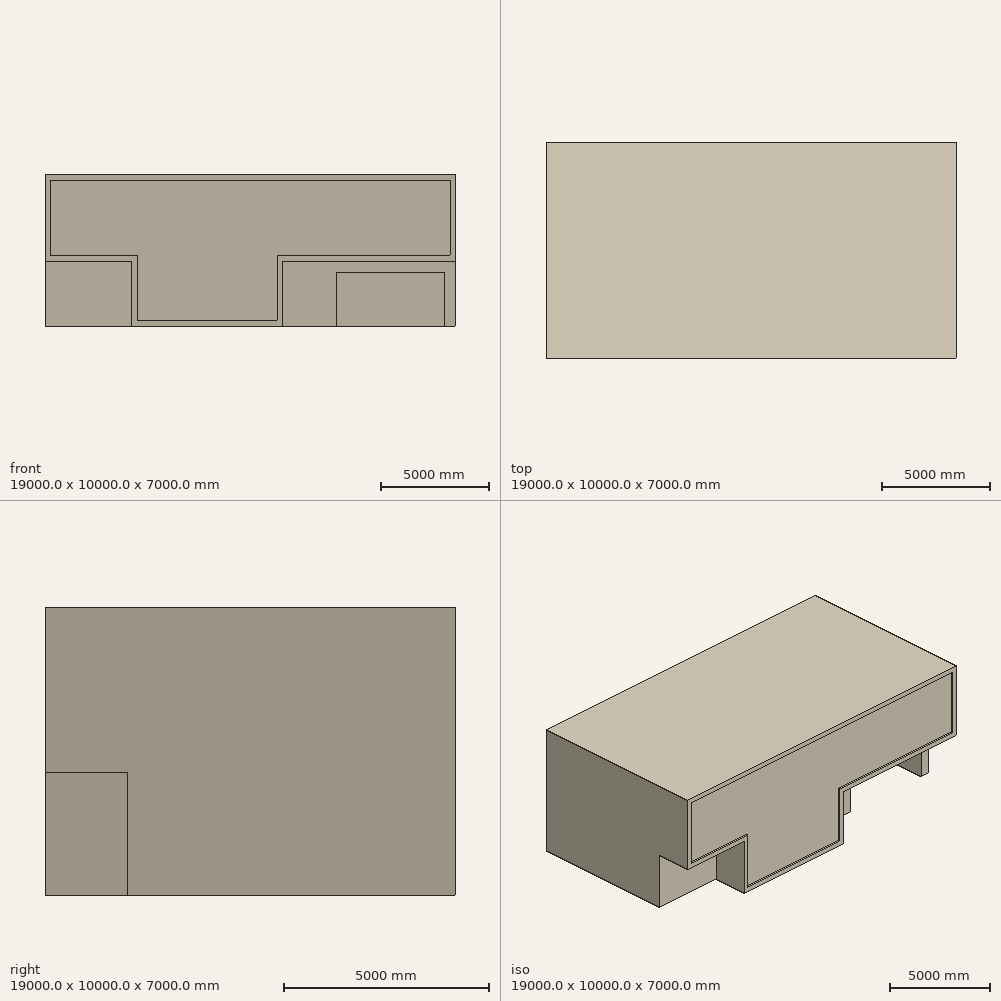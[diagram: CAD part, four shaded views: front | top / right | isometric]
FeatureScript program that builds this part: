
annotation { "Feature Type Name" : "Feature", "Feature Type Description" : "" }
export const myFeature = defineFeature(function(context is Context, id is Id, definition is map)
    precondition{}
    {
        {
            var Q0;
            Q0=qCreatedBy(makeId("Top.planeOp"),FACE);
            var sketch = newSketch(context, id + "F0", { "sketchPlane" : qUnion([Q0])});
            skLineSegment(sketch, "E0.bottom", {"start": v(9500, 5000) * mm, "end": v(-9500, 5000) * mm});
            skLineSegment(sketch, "E0.top", {"start": v(9500, -5000) * mm, "end": v(-9500, -5000) * mm});
            skLineSegment(sketch, "E0.left", {"start": v(9500, 5000) * mm, "end": v(9500, -5000) * mm});
            skLineSegment(sketch, "E0.right", {"start": v(-9500, 5000) * mm, "end": v(-9500, -5000) * mm});
            skPoint(sketch, "E0.middle", {"position": v(0, 0) * mm});
            skLineSegment(sketch, "E1.bottom", {"start": v(9500, -5000) * mm, "end": v(1500, -5000) * mm});
            skLineSegment(sketch, "E1.top", {"start": v(9500, -3000) * mm, "end": v(1500, -3000) * mm});
            skLineSegment(sketch, "E1.left", {"start": v(9500, -5000) * mm, "end": v(9500, -3000) * mm});
            skLineSegment(sketch, "E1.right", {"start": v(1500, -5000) * mm, "end": v(1500, -3000) * mm});
            skLineSegment(sketch, "E2.bottom", {"start": v(-9500, -5000) * mm, "end": v(-5500, -5000) * mm});
            skLineSegment(sketch, "E2.top", {"start": v(-9500, -3000) * mm, "end": v(-5500, -3000) * mm});
            skLineSegment(sketch, "E2.left", {"start": v(-9500, -5000) * mm, "end": v(-9500, -3000) * mm});
            skLineSegment(sketch, "E2.right", {"start": v(-5500, -5000) * mm, "end": v(-5500, -3000) * mm});
            skSolve(sketch);
        }
        {
            var Q0;
            Q0=makeQuery(id+"F0.imprint","IMPRINT",FACE,{"disambiguationData":[TD([[makeQuery(id+"F0.imprint","IMPRINT",EDGE,{"derivedFrom":sQuery(id+"F0.wireOp",EDGE,"E0.bottom")}),1.0]])]});
            extrude(context, id + "F1", {"entities" : qUnion([Q0]), "depth" : 3000 * mm, "offsetDistance" : 25 * mm});
        }
        {
            var Q0;
            Q0=makeQuery(id+"F1.opExtrude","CAP_FACE",FACE,{"disambiguationData":[OSD([sQuery(id+"F0.wireOp",EDGE,"E0.bottom"),sQuery(id+"F0.wireOp",EDGE,"E0.top"),sQuery(id+"F0.wireOp",EDGE,"E0.left"),sQuery(id+"F0.wireOp",EDGE,"E0.right"),sQuery(id+"F0.wireOp",EDGE,"E1.top"),sQuery(id+"F0.wireOp",EDGE,"E1.right"),sQuery(id+"F0.wireOp",EDGE,"E2.top"),sQuery(id+"F0.wireOp",EDGE,"E2.right")])],"isStart":false});
            var sketch = newSketch(context, id + "F2", { "sketchPlane" : qUnion([Q0])});
            skLineSegment(sketch, "E3.bottom", {"start": v(-9500, 5000) * mm, "end": v(9500, 5000) * mm});
            skLineSegment(sketch, "E3.top", {"start": v(-9500, -5000) * mm, "end": v(9500, -5000) * mm});
            skLineSegment(sketch, "E3.left", {"start": v(-9500, 5000) * mm, "end": v(-9500, -5000) * mm});
            skLineSegment(sketch, "E3.right", {"start": v(9500, 5000) * mm, "end": v(9500, -5000) * mm});
            skSolve(sketch);
        }
        {
            var Q0;
            {var subQ4=makeQuery(id+"F1.opExtrude","CAP_EDGE",EDGE,{"disambiguationData":[OSD([sQuery(id+"F0.wireOp",EDGE,"E2.top")])],"isStart":false});Q0=makeQuery(id+"F2.imprint","IMPRINT",FACE,{"disambiguationData":[TD([[makeQuery(id+"F2.imprint","IMPRINT",EDGE,{"derivedFrom":subQ4}),-1.0]])]});}
            var Q1;
            {var subQ4=makeQuery(id+"F1.opExtrude","CAP_EDGE",EDGE,{"disambiguationData":[OSD([sQuery(id+"F0.wireOp",EDGE,"E1.top")])],"isStart":false});Q1=makeQuery(id+"F2.imprint","IMPRINT",FACE,{"disambiguationData":[TD([[makeQuery(id+"F2.imprint","IMPRINT",EDGE,{"derivedFrom":subQ4}),1.0]])]});}
            var Q2;
            {var subQ1=sQuery(id+"F2.wireOp",EDGE,"E3.bottom");Q2=makeQuery(id+"F2.imprint","IMPRINT",FACE,{"disambiguationData":[TD([[makeQuery(id+"F2.imprint","IMPRINT",EDGE,{"derivedFrom":subQ1}),1.0]])]});}
            extrude(context, id + "F3", {"entities" : qUnion([Q0, Q1, Q2]), "operationType" : NewBodyOperationType.ADD, "depth" : 4000 * mm, "offsetDistance" : 25 * mm});
        }
        {
            var Q0;
            Q0=makeQuery(id+"F3.boolean.opBoolean","MERGE",FACE,{"derivedFrom":[makeQuery(id+"F1.opExtrude","SWEPT_FACE",FACE,{"disambiguationData":[OSD([sQuery(id+"F0.wireOp",EDGE,"E0.top")])]}),makeQuery(id+"F3.opExtrude","SWEPT_FACE",FACE,{"disambiguationData":[OSD([sQuery(id+"F2.wireOp",EDGE,"E3.top")])]})]});
            var sketch = newSketch(context, id + "F4", { "sketchPlane" : qUnion([Q0])});
            skLineSegment(sketch, "E4.0", {"start": v(-9500, 7000) * mm, "end": v(9500, 7000) * mm});
            skLineSegment(sketch, "E5.0", {"start": v(1500, 3000) * mm, "end": v(9500, 3000) * mm});
            skLineSegment(sketch, "E6.0", {"start": v(9500, 7000) * mm, "end": v(9500, 3000) * mm});
            skLineSegment(sketch, "E7.0", {"start": v(1500, 3000) * mm, "end": v(1500, 0) * mm});
            skLineSegment(sketch, "E8.0", {"start": v(1500, 0) * mm, "end": v(-5500, 0) * mm});
            skLineSegment(sketch, "E9.0", {"start": v(-5500, 3000) * mm, "end": v(-5500, 0) * mm});
            skLineSegment(sketch, "E10.0", {"start": v(-9500, 3000) * mm, "end": v(-5500, 3000) * mm});
            skLineSegment(sketch, "E11.0", {"start": v(-9500, 7000) * mm, "end": v(-9500, 3000) * mm});
            skLineSegment(sketch, "E12.0", {"start": v(-9250, 6750) * mm, "end": v(-9250, 3250) * mm});
            skLineSegment(sketch, "E12.1", {"start": v(-9250, 3250) * mm, "end": v(-5250, 3250) * mm});
            skLineSegment(sketch, "E12.2", {"start": v(-9250, 6750) * mm, "end": v(9250, 6750) * mm});
            skLineSegment(sketch, "E12.3", {"start": v(-5250, 3250) * mm, "end": v(-5250, 250) * mm});
            skLineSegment(sketch, "E12.4", {"start": v(9250, 6750) * mm, "end": v(9250, 3250) * mm});
            skLineSegment(sketch, "E12.5", {"start": v(1250, 3250) * mm, "end": v(9250, 3250) * mm});
            skLineSegment(sketch, "E12.6", {"start": v(1250, 3250) * mm, "end": v(1250, 250) * mm});
            skLineSegment(sketch, "E12.7", {"start": v(1250, 250) * mm, "end": v(-5250, 250) * mm});
            skSolve(sketch);
        }
        {
            var Q0;
            Q0=makeQuery(id+"F4.imprint","IMPRINT",FACE,{"disambiguationData":[TD([[makeQuery(id+"F4.imprint","IMPRINT",EDGE,{"derivedFrom":sQuery(id+"F4.wireOp",EDGE,"E12.0")}),1.0]])]});
            extrude(context, id + "F5", {"entities" : qUnion([Q0]), "operationType" : NewBodyOperationType.REMOVE, "oppositeDirection" : true, "depth" : 100 * mm, "offsetDistance" : 25 * mm});
        }
        {
            var Q0;
            Q0=makeQuery(id+"F1.opExtrude","SWEPT_FACE",FACE,{"disambiguationData":[OSD([sQuery(id+"F0.wireOp",EDGE,"E1.top")])]});
            var sketch = newSketch(context, id + "F6", { "sketchPlane" : qUnion([Q0])});
            skLineSegment(sketch, "E13.bottom", {"start": v(9000, 0) * mm, "end": v(4000, 0) * mm});
            skLineSegment(sketch, "E13.top", {"start": v(9000, 2500) * mm, "end": v(4000, 2500) * mm});
            skLineSegment(sketch, "E13.left", {"start": v(9000, 0) * mm, "end": v(9000, 2500) * mm});
            skLineSegment(sketch, "E13.right", {"start": v(4000, 0) * mm, "end": v(4000, 2500) * mm});
            skSolve(sketch);
        }
        {
            var Q0;
            Q0 = qSketchRegion(id + "F6", true);
            extrude(context, id + "F7", {"entities" : qUnion([Q0]), "operationType" : NewBodyOperationType.REMOVE, "oppositeDirection" : true, "depth" : 7600 * mm, "offsetDistance" : 25 * mm});
        }
    });
